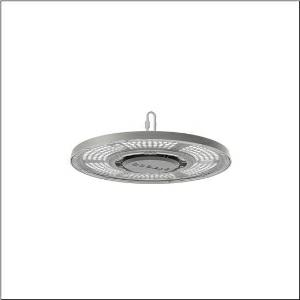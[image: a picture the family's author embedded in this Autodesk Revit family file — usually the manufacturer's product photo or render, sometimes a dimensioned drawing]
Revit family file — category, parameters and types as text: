
# Revit family: highbay_31-s_51hc41da4fmb
name_source: partatom
category: Lighting Fixtures
units: mm (PartAtom-declared; Revit-internal decimal feet)

## family parameters
Cut with Voids When Loaded = No
Host = Face
Light Source = No
Part Type = Normal
Room Calculation Point = No
Round Connector Dimension = Use Diameter
Shared = No

## types (1)
- Highbay 31-S (1 x LED, 14000 lm, 94 W, 4000K)
    Apparent Load = 94 VA
    CIE Flux Codes = 94 98 100 100 100
    Color Rendering = 80
    Color Temperature = 4000K
    Default Elevation = 1800 mm
    Description = Highbay 31-S, high bay luminaire, primary light control with lens, of PC, primary optical cover: cover panel, of PC, transparent, light emission: direct distribution, primary light characteristic: rotationally symmetric, installation type: suspended mounting, surface-mounted, LED, rated luminous flux: 14.000lm, luminous efficacy: 150lm/W, light colour: 840, colour temperature: 4000K, control gear: DALI 2, with cable, 5x 1.0mm², free wire ends, mains connection: 220..240V, AC/DC, 0/50..60Hz, cable length: 1,5m, rated input power: 94W, housing, rotationally symmetric, of diecast aluminium, powder-coated, grey aluminium (RAL 9007), with hook on luminaire side, incl. screw, diameter: 339mm, protection rating (complete): IP65, insulation class (complete): insulation class I (protective earthing), certification: CE, ENEC, UKCA, protection symbol: D, impact resistance: IK08, permissible operating ambient temperature: -30..+45°C, standard: EN 60598-2-22, EN 60598, corresponds to IFS (International Featured Standards) requirements for safety and quality in the food industry, packaging unit: 1 piece
    Height = 141 mm
    Lamp = 1 x LED
    Lamp Light Flux = 14000 lm
    Lamp Power = 94 W
    Lamp count = 1
    Length = 339 mm
    Luminous efficacy = 149 lm/W
    Manufacturer = Siteco
    ModVariant = No
    Model = 51HC41DA4FMB
    Mounting Place = Ceiling
    Mounting Type = Pendant
    Number of Poles = 1
    OnlyDefault = Yes
    Power Factor = 1
    Product Name = Highbay 31-S
    Product group = high bay luminaire
    ProductGroupID = 901
    Protection Class = Protection class I
    Protection Degree = IP 65
    RLX_Detail_Level = 1
    RLX_Emergency_Light_Flux = 0 lm
    RLX_Emergency_Type = 0
    RLX_Emergency_Type_DB = No
    RlxData = <blob elided: 106889 chars, md5=0d79698c>
    Socket = socket
    Standby Power = 0 W
    System Light Flux = 14000 lm
    System Power = 94 W
    Type Comments = Product without accessories
    Type Image = l_1007237.jpg
    URL = http://relux.com
    VarID = ---
    Voltage = 0 V
    Weight = 0.00 kg
    Width = 0 mm  [stored 0 ft]

note: [stored X ft] marks values corroborated as IEEE doubles in the binary element streams (Revit-internal decimal feet)

## geometry (parser evidence)
native form markers: Blend x4, Sweep x9
no freeform markers — native parametric forms only
